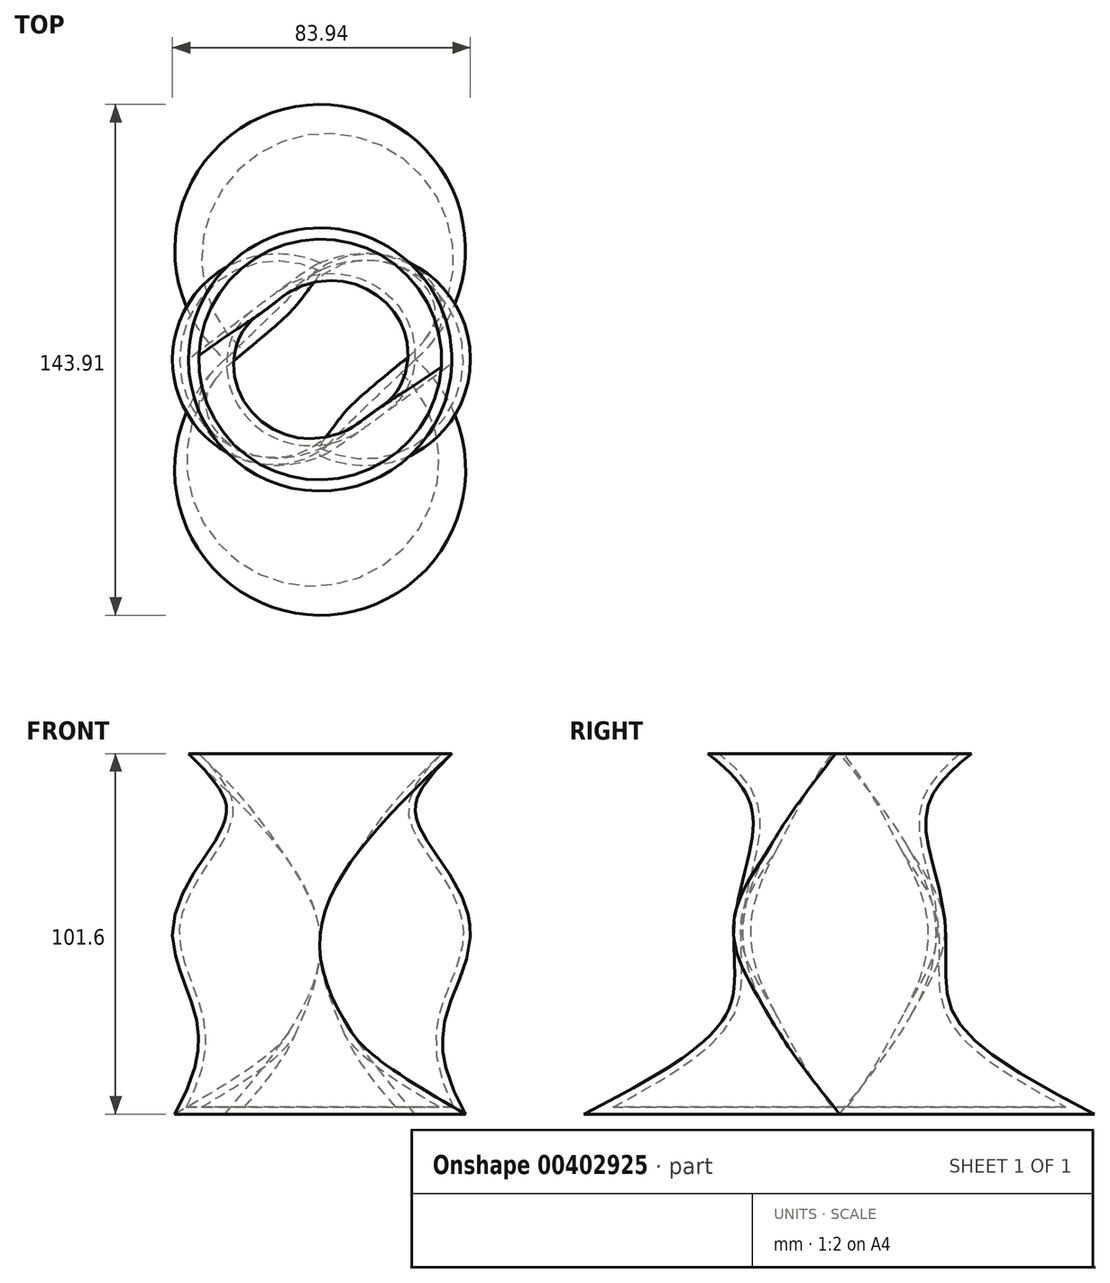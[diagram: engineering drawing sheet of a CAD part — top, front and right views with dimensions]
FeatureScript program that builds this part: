
annotation { "Feature Type Name" : "Feature", "Feature Type Description" : "" }
export const myFeature = defineFeature(function(context is Context, id is Id, definition is map)
    precondition{}
    {
        {
            var Q0;
            Q0=qCreatedBy(makeId("Top.planeOp"),FACE);
            var sketch = newSketch(context, id + "F0", { "sketchPlane" : qUnion([Q0])});
            skArc(sketch, "E0", {"start": v(26.82, 0) * mm, "mid": v(0, 71.88) * mm, "end": v(-26.82, 0) * mm});
            skArc(sketch, "E1", {"start": v(-26.82, 0) * mm, "mid": v(0, -72.03) * mm, "end": v(26.82, 0) * mm});
            skSolve(sketch);
        }
        {
            var Q0;
            Q0=qCreatedBy(makeId("Top.planeOp"),FACE);
            cPlane(context, id + "F1", {"entities" : qUnion([Q0]), "cplaneType" : CPlaneType.OFFSET, "offset" : 50.8 * mm, "width" : 152.4 * mm, "height" : 152.4 * mm});
        }
        {
            var Q0;
            Q0=qCreatedBy(id+"F1.planeOp",FACE);
            var sketch = newSketch(context, id + "F2", { "sketchPlane" : qUnion([Q0])});
            skArc(sketch, "E2", {"start": v(0, -27.2) * mm, "mid": v(42.34, 0) * mm, "end": v(0, 27.2) * mm});
            skArc(sketch, "E3", {"start": v(0, 27.2) * mm, "mid": v(-41.6, 0) * mm, "end": v(0, -27.2) * mm});
            skSolve(sketch);
        }
        {
            var Q0;
            Q0=qCreatedBy(id+"F1.planeOp",FACE);
            cPlane(context, id + "F3", {"entities" : qUnion([Q0]), "cplaneType" : CPlaneType.OFFSET, "offset" : 50.8 * mm, "width" : 152.4 * mm, "height" : 152.4 * mm});
        }
        {
            var Q0;
            Q0=qCreatedBy(id+"F3.planeOp",FACE);
            var sketch = newSketch(context, id + "F4", { "sketchPlane" : qUnion([Q0])});
            skArc(sketch, "E4", {"start": v(-37.1, 0.03) * mm, "mid": v(-0.55, -37.09) * mm, "end": v(37.08, -1.06) * mm});
            skArc(sketch, "E5", {"start": v(37.08, -1.06) * mm, "mid": v(0.55, 37.09) * mm, "end": v(-37.1, 0.03) * mm});
            skSolve(sketch);
        }
        {
            var Q0;
            Q0=makeQuery(id+"F0.imprint","IMPRINT",FACE,{"disambiguationData":[TD([[makeQuery(id+"F0.imprint","IMPRINT",EDGE,{"derivedFrom":sQuery(id+"F0.wireOp",EDGE,"E0")}),1.0]])]});
            var Q1;
            Q1=makeQuery(id+"F2.imprint","IMPRINT",FACE,{"disambiguationData":[TD([[makeQuery(id+"F2.imprint","IMPRINT",EDGE,{"derivedFrom":sQuery(id+"F2.wireOp",EDGE,"E2")}),1.0]])]});
            var Q2;
            Q2=makeQuery(id+"F4.imprint","IMPRINT",FACE,{"disambiguationData":[TD([[makeQuery(id+"F4.imprint","IMPRINT",EDGE,{"derivedFrom":sQuery(id+"F4.wireOp",EDGE,"E4")}),1.0]])]});
            loft(context, id + "F5", {"sheetProfilesArray" : [{ "sheetProfileEntities" : qUnion([Q0]) }, { "sheetProfileEntities" : qUnion([Q1]) }, { "sheetProfileEntities" : qUnion([Q2]) }]});
        }
        {
            var Q0;
            Q0=makeQuery(id+"F5.opLoft","CAP_FACE",FACE,{"disambiguationData":[OSD([makeQuery(id+"F4.imprint","IMPRINT",FACE,{"disambiguationData":[TD([[makeQuery(id+"F4.imprint","IMPRINT",EDGE,{"derivedFrom":sQuery(id+"F4.wireOp",EDGE,"E4")}),1.0]])]})])],"isStart":true});
            shell(context, id + "F6", {"entities" : qUnion([Q0]), "thickness" : 2 * mm});
        }
    });
